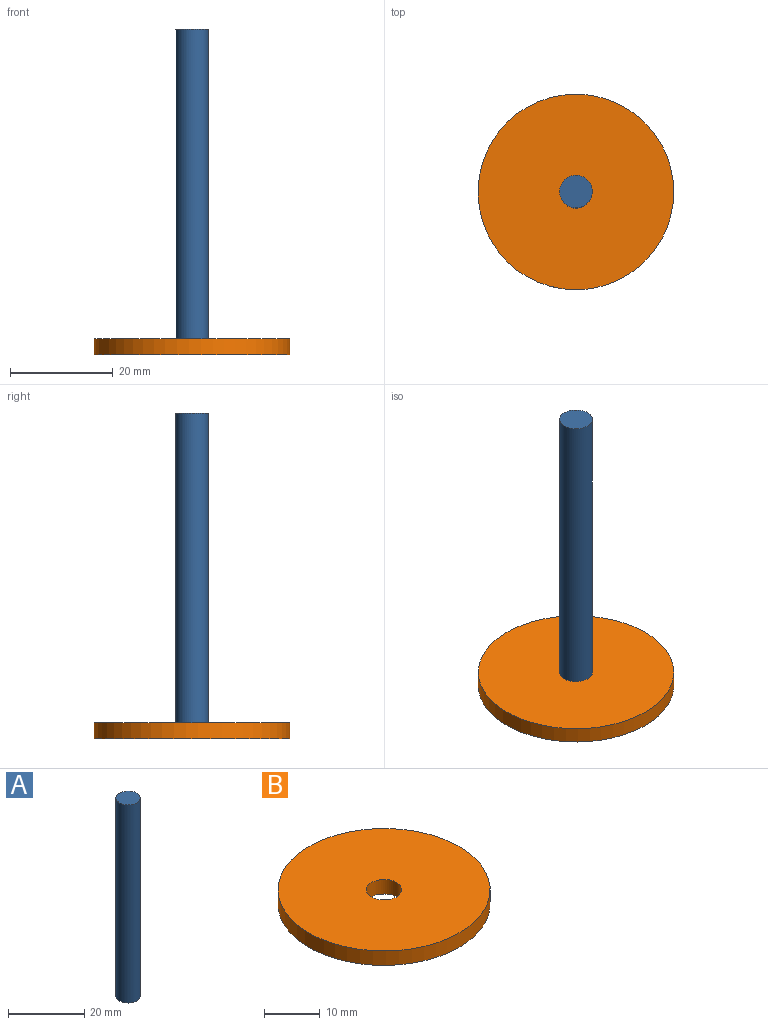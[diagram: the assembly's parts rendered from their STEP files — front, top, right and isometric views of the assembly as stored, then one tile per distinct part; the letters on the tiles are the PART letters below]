
ASSEMBLY  parts=2 mates=1
PART A: 3 faces, bbox 6.4x6.4x63.5 mm
  f0: plane 6.35x6.35mm, normal (0,0,1), area 31.7mm2, adj f1
  f1: cylinder r=3.17mm len=63.5mm, axis (0,0,-1), area 1266.8mm2, adj f0,f2
  f2: plane 6.35x6.35mm, normal (0,0,-1), area 31.7mm2, adj f1
PART B: 4 faces, bbox 38.1x38.1x3.2 mm
  f0: cylinder r=3.17mm len=6.35mm, axis (0,0,-1), area 63.3mm2, adj f2,f3
  f1: cylinder r=19.05mm len=38.1mm, axis (0,0,-1), area 380mm2, adj f2,f3
  f2: plane 38.1x38.1mm, normal (0,0,1), area 1108.4mm2, adj f0,f1
  f3: plane 38.1x38.1mm, normal (0,0,-1), area 1108.4mm2, adj f0,f1
PLACE A t=(69.85,0,-69.85)mm
PLACE B t=(69.85,0,-69.85)mm
MATE fastened B.f1 <-> A.f1  axis (0,0,-1) through (0,0,0)mm
